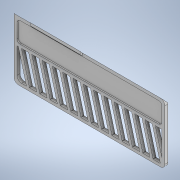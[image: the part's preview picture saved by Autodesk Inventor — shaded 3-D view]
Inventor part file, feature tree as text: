
AUTODESK INVENTOR PART (.ipt)
format: ipt  version: 2021 (Build 250183000, 183)  size: 400,384 bytes
history: native  units: mm
features: extrude x10, sketch x10, fillet x3, chamfer x1
ambient origin geometry x8: Origin, YZ Plane, XZ Plane, XY Plane, X Axis, Y Axis, Z Axis, Center Point
bodies: Solid1 (feature_tree)
feature tree (24):
  extrude  "Extrusion1"  Depth=100.0mm
  extrude  "Extrusion2"  Depth=50.0mm
  extrude  "Extrusion3"  Depth=2.0mm
  extrude  "Extrusion5"  Depth=2.0mm
  extrude  "Extrusion6"  TaperAngle=75.0deg  [1 undecoded]
  fillet  "Fillet3"  Radius=2.0mm
  extrude  "Extrusion7"  Depth=2.0mm
  fillet  "Fillet4"  Radius=2.0mm
  extrude  "Extrusion8"  Depth=2.0mm
  extrude  "Extrusion9"  Depth=2.0mm
  extrude  "Extrusion11"  Depth=2.0mm
  chamfer  "Chamfer2"  Distance=2.0mm
  extrude  "Extrusion12"  Depth=2.0mm
  fillet  "Fillet5"  Radius=2.0mm
  sketch  "Sketch1"  dims[d0=39.5mm d1=100.0mm]
  sketch  "Sketch2"  dims[d2=19.75mm d3=50.0mm]
  sketch  "Sketch3"  dims[d4=2.0mm d5=2.0mm]
  sketch  "Sketch5"  dims[d6=2.0mm d7=2.0mm]
  sketch  "Sketch6"  dims[d8=2.0mm d9=0.0mm d11=75.0deg d12=2.0mm]
  sketch  "Sketch7"  dims[d13=2.0mm d14=2.0mm d15=2.0mm]
  sketch  "Sketch8"  dims[d16=2.0mm d17=2.0mm]
  sketch  "Sketch9"  dims[d18=2.0mm d19=2.0mm]
  sketch  "Sketch11"  dims[d20=2.0mm d21=2.0mm]
  sketch  "Sketch12"  dims[d22=2.0mm d23=2.0mm d24=2.0mm d25=2.0mm d26=2.0mm d27=2.0mm d28=0.0mm d33=2.0mm d34=4.591645mm d35=5.592mm d36=2.0mm d37=0.0mm d41=2.0mm d42=0.0mm d43=300.0mm d44=0.0mm d45=3.0mm d46=3.0mm d47=3.0mm d48=300.0mm d49=0.0mm d50=3.0mm d51=20.0mm d52=2.0mm d53=0.0mm d54=97.0mm d55=0.0mm d62=12.1mm d63=33.0mm d64=1.8mm d65=2.0mm d66=1.2mm d67=0.0mm d68=1.2mm d69=2.0mm d70=8.726646mm d71=2.0mm d72=2.0mm d73=2.0mm d74=2.0mm d75=0.8mm d76=0.0mm d77=2.0mm d39=0.5mm d40=0.872665mm d60=0.5mm d61=0.872665mm]
note: 1 required parameter value undecoded (feature->parameter linkage not recoverable at this tier; creation-order binding heuristic only, values carry confidence <= 0.55)
